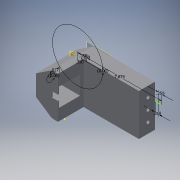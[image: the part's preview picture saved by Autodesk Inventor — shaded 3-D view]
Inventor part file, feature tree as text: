
AUTODESK INVENTOR PART (.ipt)
format: ipt  version: 2016 (Build 200138000, 138)  size: 521,728 bytes
history: native  units: in
note: dims shown in document units (in); Inventor stores cm internally (conversion verified against a paired STEP export)
features: sketch x22, extrude x18, projected_geometry x13, reference x6, plane x4, fillet x1
ambient origin geometry x8: Origin, YZ Plane, XZ Plane, XY Plane, X Axis, Y Axis, Z Axis, Center Point
bodies: Solid1 (feature_tree)
feature tree (64):
  plane  "Work Plane1"
  plane  "Work Plane2"
  sketch  "Sketch1"  dims[d0=0.1in d1=0.1in]
  plane  "Work Plane3"
  sketch  "Sketch2"  dims[d2=0.15in d3=0.35in]
  plane  "Work Plane4"
  sketch  "Sketch3"  dims[d4=0.35in d5=7.874in d6=0.0in]
  extrude  "Extrusion1"  Depth=0.1in
  extrude  "Extrusion2"  Depth=0.35in
  extrude  "Extrusion3"  Depth=0.35in
  fillet  "Fillet1"  [1 undecoded]
  extrude  "Extrusion4"  Depth=0.35in
  extrude  "Extrusion5"  TaperAngle=180.0deg  [1 undecoded]
  extrude  "Extrusion6"  Depth=0.35in
  extrude  "Extrusion7"  Depth=1.25in TaperAngle=0.0deg
  extrude  "Extrusion8"  Depth=1.25in TaperAngle=0.0deg
  extrude  "Extrusion9"  Depth=0.315in
  extrude  "Extrusion10"  Depth=0.315in TaperAngle=0.0deg
  extrude  "Extrusion11"  Depth=0.315in TaperAngle=0.0deg
  extrude  "Extrusion12"  Depth=0.2953in TaperAngle=0.0deg
  sketch  "Sketch15"  dims[d39=0.25in d40=0.0in d41=2.225in]
  sketch  "Sketch16"  dims[d42=1.9in d43=1.9in]
  extrude  "Extrusion13"  Depth=0.35in TaperAngle=0.0deg
  extrude  "Extrusion14"  Depth=0.0547in TaperAngle=0.0deg
  extrude  "Extrusion15"  Depth=0.25in
  extrude  "Extrusion16"  Depth=1.9in
  sketch  "Sketch20"  dims[d60=0.1in d61=0.0in]
  extrude  "Extrusion17"  Depth=1.378in
  extrude  "Extrusion18"  Depth=0.1181in
  reference  "Reference1"
  reference  "Reference2"
  sketch  "Sketch4"  dims[d8=0.25in d9=0.35in]
  projected_geometry  "Projected Loop1"
  sketch  "Sketch5"  dims[d10=4.61in d11=180.0deg]
  projected_geometry  "Projected Loop2"
  sketch  "Sketch6"  dims[d12=4.61in d13=0.35in]
  reference  "Reference3"
  reference  "Reference4"
  sketch  "Sketch7"  dims[d14=1.25in d15=0.0in d16=1.25in d17=0.0in]
  reference  "Reference5"
  sketch  "Sketch8"  dims[d18=0.15in d19=1.25in d20=0.0in]
  projected_geometry  "Projected Loop3"
  sketch  "Sketch9"  dims[d21=0.146in d22=0.315in]
  projected_geometry  "Projected Loop4"
  sketch  "Sketch10"  dims[d23=0.315in d24=170.0in d25=0.0in]
  projected_geometry  "Projected Loop5"
  sketch  "Sketch11"  dims[d26=0.315in d27=170.0in d28=0.0in]
  projected_geometry  "Projected Loop6"
  sketch  "Sketch12"  dims[d29=0.8661in d30=0.2953in d31=0.0in]
  projected_geometry  "Projected Loop7"
  sketch  "Sketch13"  dims[d32=0.35in d33=0.0in d34=0.3in d35=0.0in]
  sketch  "Sketch14"  dims[d36=0.315in d37=0.0547in d38=0.0in]
  projected_geometry  "Projected Loop8"
  projected_geometry  "Projected Loop9"
  sketch  "Sketch17"  dims[d44=0.689in d45=1.378in]
  projected_geometry  "Projected Loop10"
  sketch  "Sketch18"  dims[d47=0.6102in d51=0.1181in]
  projected_geometry  "Projected Loop11"
  sketch  "Sketch19"  dims[d52=0.7874in d54=1.2205in d55=0.7874in d57=1.2205in]
  reference  "Reference6"
  sketch  "Sketch21"  dims[d62=0.1in d63=0.0in]
  projected_geometry  "Projected Loop12"
  sketch  "Sketch22"  dims[d64=1.9685in d65=0.0in d66=0.8268in d67=0.0in d68=0.325in d69=0.0in d70=1.9685in d71=0.0in d72=0.325in d73=0.0in d74=1.7717in d75=0.325in d76=0.0in d77=1.7323in d78=1.975in d79=0.0in d80=0.1in d81=0.0in d82=1.1811in d83=0.5118in d84=0.2875in d85=0.0in]
  projected_geometry  "Projected Loop13"
note: 2 required parameter values undecoded (feature->parameter linkage not recoverable at this tier; creation-order binding heuristic only, values carry confidence <= 0.55)
